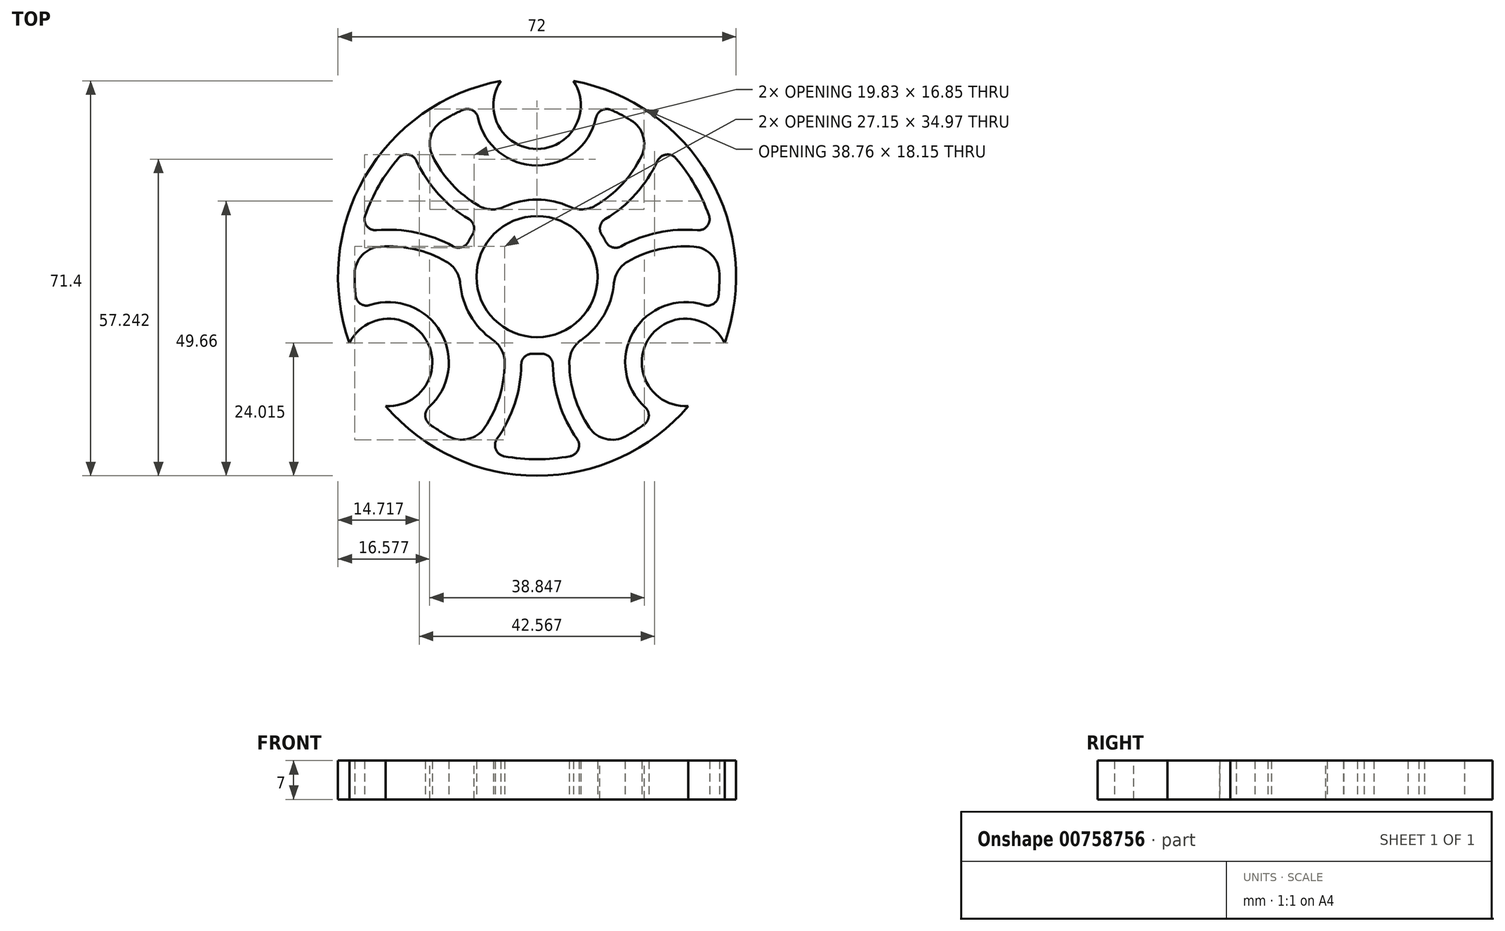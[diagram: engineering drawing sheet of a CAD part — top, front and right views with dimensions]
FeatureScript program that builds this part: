
annotation { "Feature Type Name" : "Feature", "Feature Type Description" : "" }
export const myFeature = defineFeature(function(context is Context, id is Id, definition is map)
    precondition{}
    {
        {
            var Q0;
            Q0=qCreatedBy(makeId("Top.planeOp"),FACE);
            var sketch = newSketch(context, id + "F0", { "sketchPlane" : qUnion([Q0])});
            skCircle(sketch, "E0", {"center": v(0, 0) * mm, "radius": 10.95 * mm});
            skArc(sketch, "E1", {"start": v(-2.92, -13.64) * mm, "mid": v(0, -13.95) * mm, "end": v(2.92, -13.64) * mm});
            skArc(sketch, "E2", {"start": v(-6.56, 35.4) * mm, "mid": v(0, 23.1) * mm, "end": v(6.56, 35.4) * mm});
            skArc(sketch, "E3.1.1", {"start": v(-27.37, -23.38) * mm, "mid": v(-20, -11.55) * mm, "end": v(-33.94, -12.01) * mm});
            skArc(sketch, "E3.2.1", {"start": v(33.94, -12.01) * mm, "mid": v(20, -11.55) * mm, "end": v(27.37, -23.38) * mm});
            skArc(sketch, "E4", {"start": v(-27.37, -23.38) * mm, "mid": v(0, -36) * mm, "end": v(27.37, -23.38) * mm});
            skArc(sketch, "E5", {"start": v(-21.53, -25.01) * mm, "mid": v(-17.14, -28.2) * mm, "end": v(-12.28, -30.63) * mm});
            skArc(sketch, "E6", {"start": v(-10.9, 31.15) * mm, "mid": v(0, 20.1) * mm, "end": v(10.9, 31.15) * mm});
            skArc(sketch, "E7", {"start": v(32.42, -6.14) * mm, "mid": v(17.4, -10.05) * mm, "end": v(21.53, -25.01) * mm});
            skArc(sketch, "E8", {"start": v(-21.53, -25.01) * mm, "mid": v(-17.4, -10.05) * mm, "end": v(-32.42, -6.14) * mm});
            skArc(sketch, "E9.trimOffspring", {"start": v(32.42, -6.14) * mm, "mid": v(31.44, 10.03) * mm, "end": v(22.89, 23.77) * mm});
            skArc(sketch, "E10.trimOffspring", {"start": v(33.94, -12.01) * mm, "mid": v(31.18, 18) * mm, "end": v(6.56, 35.4) * mm});
            skArc(sketch, "E11.trimOffspring", {"start": v(-6.56, 35.4) * mm, "mid": v(-31.18, 18) * mm, "end": v(-33.94, -12.01) * mm});
            skArc(sketch, "E12.trimOffspring", {"start": v(-10.9, 31.15) * mm, "mid": v(-15.86, 28.94) * mm, "end": v(-20.38, 25.95) * mm});
            skLineSegment(sketch, "E13", {"start": v(0, 31) * mm, "end": v(0, 0) * mm, "construction": true});
            skLineSegment(sketch, "E14", {"start": v(26.85, -15.5) * mm, "end": v(0, 0) * mm, "construction": true});
            skLineSegment(sketch, "E15", {"start": v(-26.85, -15.5) * mm, "end": v(0, 0) * mm, "construction": true});
            skArc(sketch, "E16", {"start": v(-12.28, -30.63) * mm, "mid": v(-7, -22.35) * mm, "end": v(-6.05, -12.57) * mm});
            skArc(sketch, "E17", {"start": v(-9.15, -31.7) * mm, "mid": v(-4.16, -23.32) * mm, "end": v(-2.92, -13.64) * mm});
            skArc(sketch, "E18.trimOffspring", {"start": v(-9.15, -31.7) * mm, "mid": v(0, -33) * mm, "end": v(9.15, -31.7) * mm});
            skArc(sketch, "E19.trimOffspring", {"start": v(-13.91, 1.04) * mm, "mid": v(-22.85, 5.12) * mm, "end": v(-32.67, 4.68) * mm});
            skArc(sketch, "E20.trimOffspring", {"start": v(-13.27, 4.3) * mm, "mid": v(-22.27, 8.06) * mm, "end": v(-32.03, 7.93) * mm});
            skArc(sketch, "E21.trimOffspring", {"start": v(-13.91, 1.04) * mm, "mid": v(-12.08, -6.98) * mm, "end": v(-6.05, -12.57) * mm});
            skArc(sketch, "E22.trimOffspring", {"start": v(-32.67, 4.68) * mm, "mid": v(-33, -0.74) * mm, "end": v(-32.42, -6.14) * mm});
            skArc(sketch, "E23", {"start": v(32.03, 7.93) * mm, "mid": v(22.27, 8.06) * mm, "end": v(13.27, 4.3) * mm});
            skArc(sketch, "E24", {"start": v(32.67, 4.68) * mm, "mid": v(22.85, 5.12) * mm, "end": v(13.91, 1.04) * mm});
            skArc(sketch, "E25.trimOffspring", {"start": v(12.28, -30.63) * mm, "mid": v(17.14, -28.2) * mm, "end": v(21.53, -25.01) * mm});
            skArc(sketch, "E26.trimOffspring", {"start": v(13.27, 4.3) * mm, "mid": v(12.08, 6.97) * mm, "end": v(10.35, 9.35) * mm});
            skArc(sketch, "E27.trimOffspring", {"start": v(2.92, -13.64) * mm, "mid": v(4.16, -23.32) * mm, "end": v(9.15, -31.7) * mm});
            skArc(sketch, "E28.trimOffspring", {"start": v(6.05, -12.57) * mm, "mid": v(7, -22.35) * mm, "end": v(12.28, -30.63) * mm});
            skArc(sketch, "E29.trimOffspring", {"start": v(6.05, -12.57) * mm, "mid": v(12.08, -6.98) * mm, "end": v(13.91, 1.04) * mm});
            skArc(sketch, "E30", {"start": v(-20.38, 25.95) * mm, "mid": v(-15.86, 17.23) * mm, "end": v(-7.86, 11.53) * mm});
            skArc(sketch, "E31", {"start": v(-22.89, 23.77) * mm, "mid": v(-18.12, 15.26) * mm, "end": v(-10.35, 9.35) * mm});
            skArc(sketch, "E32.trimOffspring", {"start": v(-22.89, 23.77) * mm, "mid": v(-28.58, 16.5) * mm, "end": v(-32.03, 7.93) * mm});
            skArc(sketch, "E33.trimOffspring", {"start": v(7.86, 11.53) * mm, "mid": v(15.86, 17.23) * mm, "end": v(20.38, 25.95) * mm});
            skArc(sketch, "E34.trimOffspring", {"start": v(-10.35, 9.35) * mm, "mid": v(-12.08, 6.98) * mm, "end": v(-13.27, 4.3) * mm});
            skArc(sketch, "E35.trimOffspring", {"start": v(10.35, 9.35) * mm, "mid": v(18.12, 15.26) * mm, "end": v(22.89, 23.77) * mm});
            skArc(sketch, "E36.trimOffspring", {"start": v(7.86, 11.53) * mm, "mid": v(0, 13.95) * mm, "end": v(-7.86, 11.53) * mm});
            skArc(sketch, "E37.trimOffspring", {"start": v(20.38, 25.95) * mm, "mid": v(15.86, 28.94) * mm, "end": v(10.9, 31.15) * mm});
            skSolve(sketch);
        }
        {
            var Q0;
            Q0=makeQuery(id+"F0.imprint","IMPRINT",FACE,{"disambiguationData":[TD([[makeQuery(id+"F0.imprint","IMPRINT",EDGE,{"derivedFrom":sQuery(id+"F0.wireOp",EDGE,"E0")}),-1.0]])]});
            var Q1;
            Q1=makeQuery(id+"F0.imprint","IMPRINT",FACE,{"disambiguationData":[TD([[makeQuery(id+"F0.imprint","IMPRINT",EDGE,{"derivedFrom":sQuery(id+"F0.wireOp",EDGE,"E2")}),-1.0]])]});
            extrude(context, id + "F1", {"entities" : qUnion([Q0, Q1]), "depth" : 7 * mm, "offsetDistance" : 25 * mm});
        }
        {
            var Q0;
            Q0=makeQuery(id+"F1.opExtrude","SWEPT_EDGE",EDGE,{"disambiguationData":[OSD([sQuery(id+"F0.wireOp",EDGE,"E28.trimOffspring"),sQuery(id+"F0.wireOp",EDGE,"E29.trimOffspring")])]});
            var Q1;
            Q1=makeQuery(id+"F1.opExtrude","SWEPT_EDGE",EDGE,{"disambiguationData":[OSD([sQuery(id+"F0.wireOp",EDGE,"E24"),sQuery(id+"F0.wireOp",EDGE,"E29.trimOffspring")])]});
            var Q2;
            Q2=makeQuery(id+"F1.opExtrude","SWEPT_EDGE",EDGE,{"disambiguationData":[OSD([sQuery(id+"F0.wireOp",EDGE,"E33.trimOffspring"),sQuery(id+"F0.wireOp",EDGE,"E36.trimOffspring")])]});
            var Q3;
            Q3=makeQuery(id+"F1.opExtrude","SWEPT_EDGE",EDGE,{"disambiguationData":[OSD([sQuery(id+"F0.wireOp",EDGE,"E30"),sQuery(id+"F0.wireOp",EDGE,"E36.trimOffspring")])]});
            var Q4;
            Q4=makeQuery(id+"F1.opExtrude","SWEPT_EDGE",EDGE,{"disambiguationData":[OSD([sQuery(id+"F0.wireOp",EDGE,"E19.trimOffspring"),sQuery(id+"F0.wireOp",EDGE,"E21.trimOffspring")])]});
            var Q5;
            Q5=makeQuery(id+"F1.opExtrude","SWEPT_EDGE",EDGE,{"disambiguationData":[OSD([sQuery(id+"F0.wireOp",EDGE,"E16"),sQuery(id+"F0.wireOp",EDGE,"E21.trimOffspring")])]});
            var Q6;
            Q6=makeQuery(id+"F1.opExtrude","SWEPT_EDGE",EDGE,{"disambiguationData":[OSD([sQuery(id+"F0.wireOp",EDGE,"E12.trimOffspring"),sQuery(id+"F0.wireOp",EDGE,"E30")])]});
            var Q7;
            Q7=makeQuery(id+"F1.opExtrude","SWEPT_EDGE",EDGE,{"disambiguationData":[OSD([sQuery(id+"F0.wireOp",EDGE,"E19.trimOffspring"),sQuery(id+"F0.wireOp",EDGE,"E22.trimOffspring")])]});
            var Q8;
            Q8=makeQuery(id+"F1.opExtrude","SWEPT_EDGE",EDGE,{"disambiguationData":[OSD([sQuery(id+"F0.wireOp",EDGE,"E5"),sQuery(id+"F0.wireOp",EDGE,"E16")])]});
            var Q9;
            Q9=makeQuery(id+"F1.opExtrude","SWEPT_EDGE",EDGE,{"disambiguationData":[OSD([sQuery(id+"F0.wireOp",EDGE,"E25.trimOffspring"),sQuery(id+"F0.wireOp",EDGE,"E28.trimOffspring")])]});
            var Q10;
            Q10=makeQuery(id+"F1.opExtrude","SWEPT_EDGE",EDGE,{"disambiguationData":[OSD([sQuery(id+"F0.wireOp",EDGE,"E9.trimOffspring"),sQuery(id+"F0.wireOp",EDGE,"E24")])]});
            var Q11;
            Q11=makeQuery(id+"F1.opExtrude","SWEPT_EDGE",EDGE,{"disambiguationData":[OSD([sQuery(id+"F0.wireOp",EDGE,"E33.trimOffspring"),sQuery(id+"F0.wireOp",EDGE,"E37.trimOffspring")])]});
            fillet(context, id + "F2", {"entities" : qUnion([Q0, Q1, Q2, Q3, Q4, Q5, Q6, Q7, Q8, Q9, Q10, Q11]), "radius" : 5 * mm, "tangentPropagation" : true, "allowEdgeOverflow" : false});
        }
        {
            var Q0;
            Q0=makeQuery(id+"F1.opExtrude","SWEPT_EDGE",EDGE,{"disambiguationData":[OSD([sQuery(id+"F0.wireOp",EDGE,"E20.trimOffspring"),sQuery(id+"F0.wireOp",EDGE,"E32.trimOffspring")])]});
            var Q1;
            Q1=makeQuery(id+"F1.opExtrude","SWEPT_EDGE",EDGE,{"disambiguationData":[OSD([sQuery(id+"F0.wireOp",EDGE,"E31"),sQuery(id+"F0.wireOp",EDGE,"E32.trimOffspring")])]});
            var Q2;
            Q2=makeQuery(id+"F1.opExtrude","SWEPT_EDGE",EDGE,{"disambiguationData":[OSD([sQuery(id+"F0.wireOp",EDGE,"E20.trimOffspring"),sQuery(id+"F0.wireOp",EDGE,"E34.trimOffspring")])]});
            var Q3;
            Q3=makeQuery(id+"F1.opExtrude","SWEPT_EDGE",EDGE,{"disambiguationData":[OSD([sQuery(id+"F0.wireOp",EDGE,"E31"),sQuery(id+"F0.wireOp",EDGE,"E34.trimOffspring")])]});
            var Q4;
            Q4=makeQuery(id+"F1.opExtrude","SWEPT_EDGE",EDGE,{"disambiguationData":[OSD([sQuery(id+"F0.wireOp",EDGE,"E23"),sQuery(id+"F0.wireOp",EDGE,"E26.trimOffspring")])]});
            var Q5;
            Q5=makeQuery(id+"F1.opExtrude","SWEPT_EDGE",EDGE,{"disambiguationData":[OSD([sQuery(id+"F0.wireOp",EDGE,"E26.trimOffspring"),sQuery(id+"F0.wireOp",EDGE,"E35.trimOffspring")])]});
            var Q6;
            Q6=makeQuery(id+"F1.opExtrude","SWEPT_EDGE",EDGE,{"disambiguationData":[OSD([sQuery(id+"F0.wireOp",EDGE,"E9.trimOffspring"),sQuery(id+"F0.wireOp",EDGE,"E35.trimOffspring")])]});
            var Q7;
            Q7=makeQuery(id+"F1.opExtrude","SWEPT_EDGE",EDGE,{"disambiguationData":[OSD([sQuery(id+"F0.wireOp",EDGE,"E9.trimOffspring"),sQuery(id+"F0.wireOp",EDGE,"E23")])]});
            var Q8;
            Q8=makeQuery(id+"F1.opExtrude","SWEPT_EDGE",EDGE,{"disambiguationData":[OSD([sQuery(id+"F0.wireOp",EDGE,"E7"),sQuery(id+"F0.wireOp",EDGE,"E9.trimOffspring")])]});
            var Q9;
            Q9=makeQuery(id+"F1.opExtrude","SWEPT_EDGE",EDGE,{"disambiguationData":[OSD([sQuery(id+"F0.wireOp",EDGE,"E6"),sQuery(id+"F0.wireOp",EDGE,"E37.trimOffspring")])]});
            var Q10;
            Q10=makeQuery(id+"F1.opExtrude","SWEPT_EDGE",EDGE,{"disambiguationData":[OSD([sQuery(id+"F0.wireOp",EDGE,"E6"),sQuery(id+"F0.wireOp",EDGE,"E12.trimOffspring")])]});
            var Q11;
            Q11=makeQuery(id+"F1.opExtrude","SWEPT_EDGE",EDGE,{"disambiguationData":[OSD([sQuery(id+"F0.wireOp",EDGE,"E8"),sQuery(id+"F0.wireOp",EDGE,"E22.trimOffspring")])]});
            var Q12;
            Q12=makeQuery(id+"F1.opExtrude","SWEPT_EDGE",EDGE,{"disambiguationData":[OSD([sQuery(id+"F0.wireOp",EDGE,"E5"),sQuery(id+"F0.wireOp",EDGE,"E8")])]});
            var Q13;
            Q13=makeQuery(id+"F1.opExtrude","SWEPT_EDGE",EDGE,{"disambiguationData":[OSD([sQuery(id+"F0.wireOp",EDGE,"E17"),sQuery(id+"F0.wireOp",EDGE,"E18.trimOffspring")])]});
            var Q14;
            Q14=makeQuery(id+"F1.opExtrude","SWEPT_EDGE",EDGE,{"disambiguationData":[OSD([sQuery(id+"F0.wireOp",EDGE,"E1"),sQuery(id+"F0.wireOp",EDGE,"E27.trimOffspring")])]});
            var Q15;
            Q15=makeQuery(id+"F1.opExtrude","SWEPT_EDGE",EDGE,{"disambiguationData":[OSD([sQuery(id+"F0.wireOp",EDGE,"E1"),sQuery(id+"F0.wireOp",EDGE,"E17")])]});
            var Q16;
            Q16=makeQuery(id+"F1.opExtrude","SWEPT_EDGE",EDGE,{"disambiguationData":[OSD([sQuery(id+"F0.wireOp",EDGE,"E7"),sQuery(id+"F0.wireOp",EDGE,"E25.trimOffspring")])]});
            var Q17;
            Q17=makeQuery(id+"F1.opExtrude","SWEPT_EDGE",EDGE,{"disambiguationData":[OSD([sQuery(id+"F0.wireOp",EDGE,"E18.trimOffspring"),sQuery(id+"F0.wireOp",EDGE,"E27.trimOffspring")])]});
            fillet(context, id + "F3", {"entities" : qUnion([Q0, Q1, Q2, Q3, Q4, Q5, Q6, Q7, Q8, Q9, Q10, Q11, Q12, Q13, Q14, Q15, Q16, Q17]), "radius" : 2 * mm, "tangentPropagation" : true, "allowEdgeOverflow" : false});
        }
    });
